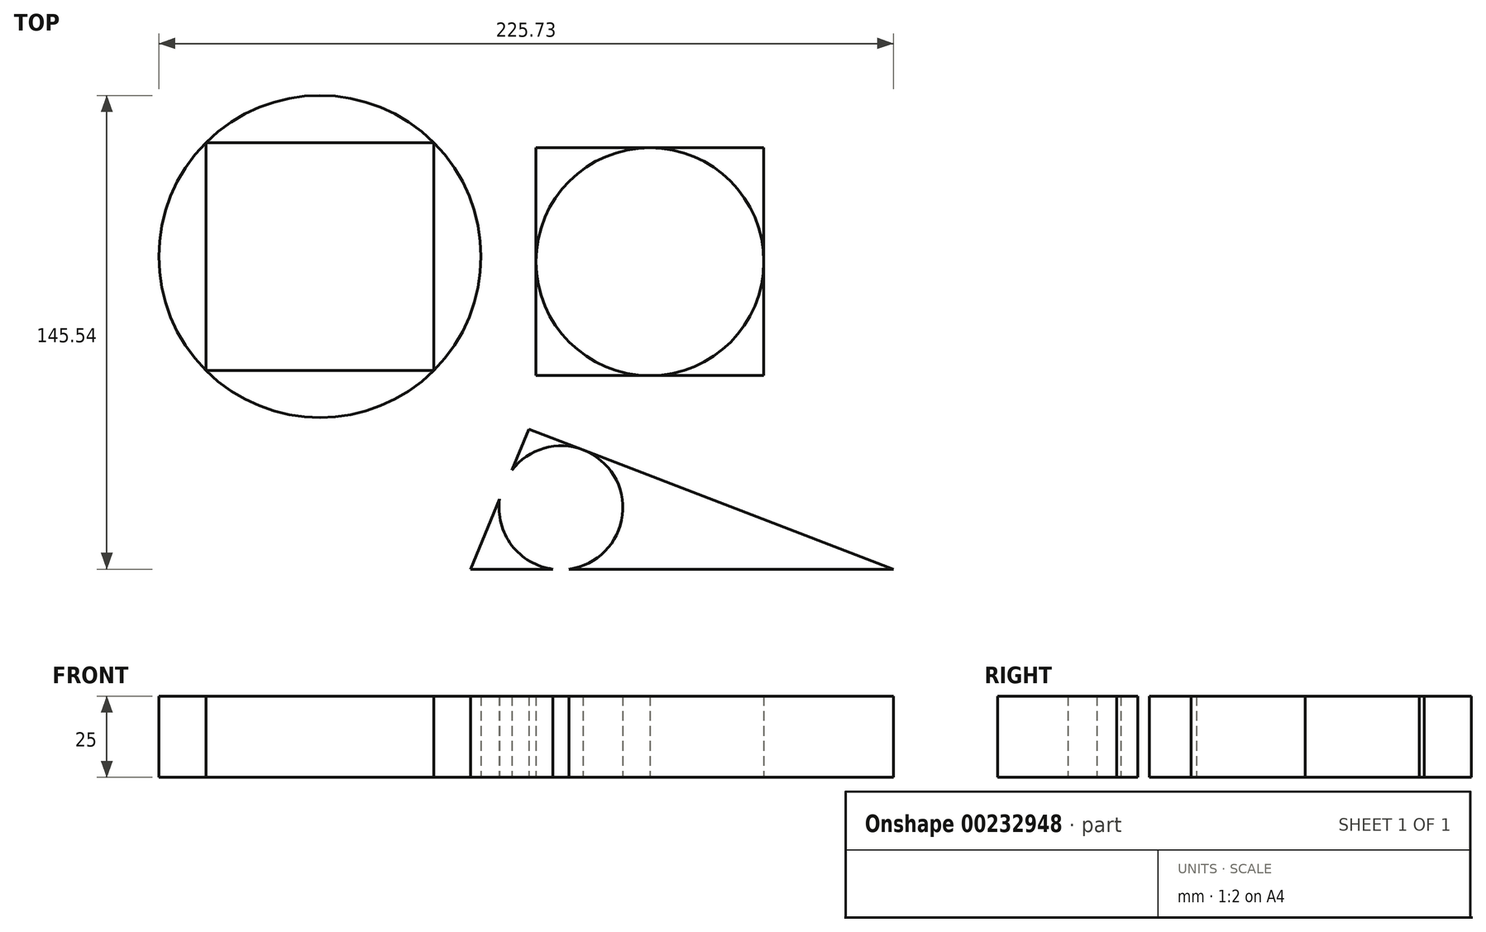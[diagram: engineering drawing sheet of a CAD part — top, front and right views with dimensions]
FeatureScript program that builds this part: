
annotation { "Feature Type Name" : "Feature", "Feature Type Description" : "" }
export const myFeature = defineFeature(function(context is Context, id is Id, definition is map)
    precondition{}
    {
        {
            var Q0;
            Q0=qCreatedBy(makeId("Top.planeOp"),FACE);
            var sketch = newSketch(context, id + "F0", { "sketchPlane" : qUnion([Q0])});
            skLineSegment(sketch, "E0", {"start": v(0, 70) * mm, "end": v(70, 70) * mm});
            skLineSegment(sketch, "E1", {"start": v(70, 70) * mm, "end": v(70, 0) * mm});
            skLineSegment(sketch, "E2", {"start": v(70, 0) * mm, "end": v(0, 0) * mm});
            skLineSegment(sketch, "E3", {"start": v(0, 0) * mm, "end": v(0, 70) * mm});
            skLineSegment(sketch, "E4", {"start": v(0, 70) * mm, "end": v(70, 0) * mm, "construction": true});
            skLineSegment(sketch, "E5", {"start": v(70, 70) * mm, "end": v(0, 0) * mm, "construction": true});
            skCircle(sketch, "E6", {"center": v(35, 35) * mm, "radius": 35 * mm});
            skLineSegment(sketch, "E7", {"start": v(-31.39, 71.59) * mm, "end": v(-101.39, 71.59) * mm});
            skLineSegment(sketch, "E8", {"start": v(-101.39, 71.59) * mm, "end": v(-101.39, 1.59) * mm});
            skLineSegment(sketch, "E9", {"start": v(-101.39, 1.59) * mm, "end": v(-31.39, 1.59) * mm});
            skLineSegment(sketch, "E10", {"start": v(-31.39, 1.59) * mm, "end": v(-31.39, 71.59) * mm});
            skLineSegment(sketch, "E11", {"start": v(-101.39, 1.59) * mm, "end": v(-31.39, 71.59) * mm, "construction": true});
            skLineSegment(sketch, "E12", {"start": v(-101.39, 71.59) * mm, "end": v(-31.39, 1.59) * mm, "construction": true});
            skCircle(sketch, "E13", {"center": v(-66.39, 36.59) * mm, "radius": 49.5 * mm});
            skLineSegment(sketch, "E14", {"start": v(-20.15, -59.46) * mm, "end": v(109.85, -59.46) * mm});
            skLineSegment(sketch, "E15", {"start": v(109.85, -59.46) * mm, "end": v(-2.18, -16.45) * mm});
            skLineSegment(sketch, "E16", {"start": v(-20.15, -59.46) * mm, "end": v(-2.18, -16.45) * mm});
            skCircle(sketch, "E17", {"center": v(7.67, -40.6) * mm, "radius": 19.02 * mm});
            skPoint(sketch, "E17.first.point", {"position": v(14.48, -22.85) * mm});
            skPoint(sketch, "E17.second.point", {"position": v(-11.16, -37.95) * mm});
            skPoint(sketch, "E17.third.point", {"position": v(5.21, -59.46) * mm});
            skSolve(sketch);
        }
        {
            var Q0;
            {var subQ0=sQuery(id+"F0.wireOp",EDGE,"E3");var subQ1=sQuery(id+"F0.wireOp",EDGE,"E0");var subQ2=makeQuery(id+"F0.imprint","INTERSECT",VERTEX,{"derivedFrom":[subQ1,subQ0]});Q0=makeQuery(id+"F0.imprint","IMPRINT",FACE,{"disambiguationData":[TD([[makeQuery(id+"F0.imprint","IMPRINT",EDGE,{"disambiguationData":[TD([[subQ2,-1.0]])],"derivedFrom":subQ1}),-1.0]])]});}
            var Q1;
            {var subQ0=sQuery(id+"F0.wireOp",EDGE,"E1");var subQ1=sQuery(id+"F0.wireOp",EDGE,"E0");var subQ2=makeQuery(id+"F0.imprint","INTERSECT",VERTEX,{"derivedFrom":[subQ1,subQ0]});Q1=makeQuery(id+"F0.imprint","IMPRINT",FACE,{"disambiguationData":[TD([[makeQuery(id+"F0.imprint","IMPRINT",EDGE,{"disambiguationData":[TD([[subQ2,1.0]])],"derivedFrom":subQ1}),-1.0]])]});}
            var Q2;
            {var subQ0=sQuery(id+"F0.wireOp",EDGE,"E2");var subQ1=sQuery(id+"F0.wireOp",EDGE,"E1");var subQ2=makeQuery(id+"F0.imprint","INTERSECT",VERTEX,{"derivedFrom":[subQ1,subQ0]});Q2=makeQuery(id+"F0.imprint","IMPRINT",FACE,{"disambiguationData":[TD([[makeQuery(id+"F0.imprint","IMPRINT",EDGE,{"disambiguationData":[TD([[subQ2,1.0]])],"derivedFrom":subQ1}),-1.0]])]});}
            var Q3;
            {var subQ0=sQuery(id+"F0.wireOp",EDGE,"E3");var subQ1=sQuery(id+"F0.wireOp",EDGE,"E2");var subQ2=makeQuery(id+"F0.imprint","INTERSECT",VERTEX,{"derivedFrom":[subQ1,subQ0]});Q3=makeQuery(id+"F0.imprint","IMPRINT",FACE,{"disambiguationData":[TD([[makeQuery(id+"F0.imprint","IMPRINT",EDGE,{"disambiguationData":[TD([[subQ2,1.0]])],"derivedFrom":subQ1}),-1.0]])]});}
            var Q4;
            {var subQ0=sQuery(id+"F0.wireOp",EDGE,"E7");Q4=makeQuery(id+"F0.imprint","IMPRINT",FACE,{"disambiguationData":[TD([[makeQuery(id+"F0.imprint","IMPRINT",EDGE,{"derivedFrom":subQ0}),-1.0]])]});}
            var Q5;
            {var subQ0=sQuery(id+"F0.wireOp",EDGE,"E8");Q5=makeQuery(id+"F0.imprint","IMPRINT",FACE,{"disambiguationData":[TD([[makeQuery(id+"F0.imprint","IMPRINT",EDGE,{"derivedFrom":subQ0}),-1.0]])]});}
            var Q6;
            {var subQ0=sQuery(id+"F0.wireOp",EDGE,"E9");Q6=makeQuery(id+"F0.imprint","IMPRINT",FACE,{"disambiguationData":[TD([[makeQuery(id+"F0.imprint","IMPRINT",EDGE,{"derivedFrom":subQ0}),-1.0]])]});}
            var Q7;
            {var subQ0=sQuery(id+"F0.wireOp",EDGE,"E10");Q7=makeQuery(id+"F0.imprint","IMPRINT",FACE,{"disambiguationData":[TD([[makeQuery(id+"F0.imprint","IMPRINT",EDGE,{"derivedFrom":subQ0}),-1.0]])]});}
            var Q8;
            {var subQ0=sQuery(id+"F0.wireOp",EDGE,"E16");var subQ1=sQuery(id+"F0.wireOp",EDGE,"E14");var subQ2=makeQuery(id+"F0.imprint","INTERSECT",VERTEX,{"derivedFrom":[subQ1,subQ0]});Q8=makeQuery(id+"F0.imprint","IMPRINT",FACE,{"disambiguationData":[TD([[makeQuery(id+"F0.imprint","IMPRINT",EDGE,{"disambiguationData":[TD([[subQ2,-1.0]])],"derivedFrom":subQ1}),1.0]])]});}
            var Q9;
            {var subQ0=sQuery(id+"F0.wireOp",EDGE,"E17");var subQ1=sQuery(id+"F0.wireOp",EDGE,"E14");var subQ2=makeQuery(id+"F0.imprint","INTERSECT",VERTEX,{"disambiguationData":[OD(0.0)],"derivedFrom":[subQ1,subQ0]});Q9=makeQuery(id+"F0.imprint","IMPRINT",FACE,{"disambiguationData":[TD([[makeQuery(id+"F0.imprint","IMPRINT",EDGE,{"disambiguationData":[TD([[subQ2,-1.0]])],"derivedFrom":subQ1}),-1.0]])]});}
            var Q10;
            {var subQ0=sQuery(id+"F0.wireOp",EDGE,"E15");var subQ1=sQuery(id+"F0.wireOp",EDGE,"E14");var subQ2=makeQuery(id+"F0.imprint","INTERSECT",VERTEX,{"derivedFrom":[subQ1,subQ0]});Q10=makeQuery(id+"F0.imprint","IMPRINT",FACE,{"disambiguationData":[TD([[makeQuery(id+"F0.imprint","IMPRINT",EDGE,{"disambiguationData":[TD([[subQ2,1.0]])],"derivedFrom":subQ1}),1.0]])]});}
            var Q11;
            {var subQ0=sQuery(id+"F0.wireOp",EDGE,"E16");var subQ1=sQuery(id+"F0.wireOp",EDGE,"E15");var subQ2=makeQuery(id+"F0.imprint","INTERSECT",VERTEX,{"derivedFrom":[subQ1,subQ0]});Q11=makeQuery(id+"F0.imprint","IMPRINT",FACE,{"disambiguationData":[TD([[makeQuery(id+"F0.imprint","IMPRINT",EDGE,{"disambiguationData":[TD([[subQ2,1.0]])],"derivedFrom":subQ1}),1.0]])]});}
            var Q12;
            {var subQ0=sQuery(id+"F0.wireOp",EDGE,"E17");var subQ1=sQuery(id+"F0.wireOp",EDGE,"E16");var subQ2=makeQuery(id+"F0.imprint","INTERSECT",VERTEX,{"disambiguationData":[OD(0.0)],"derivedFrom":[subQ1,subQ0]});Q12=makeQuery(id+"F0.imprint","IMPRINT",FACE,{"disambiguationData":[TD([[makeQuery(id+"F0.imprint","IMPRINT",EDGE,{"disambiguationData":[TD([[subQ2,-1.0]])],"derivedFrom":subQ1}),1.0]])]});}
            extrude(context, id + "F1", {"entities" : qUnion([Q0, Q1, Q2, Q3, Q4, Q5, Q6, Q7, Q8, Q9, Q10, Q11, Q12]), "depth" : 25 * mm});
        }
    });
